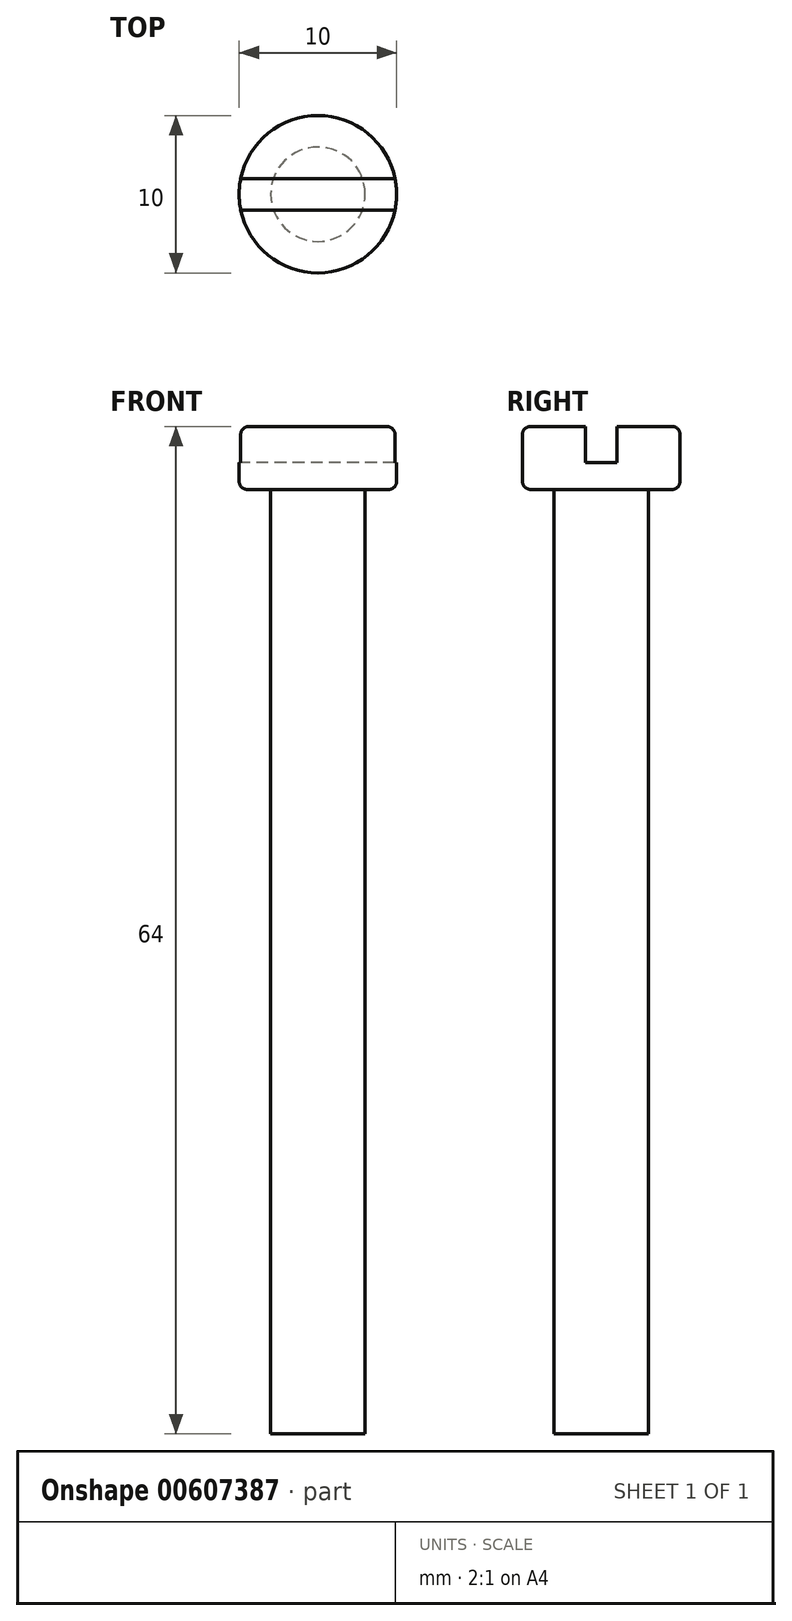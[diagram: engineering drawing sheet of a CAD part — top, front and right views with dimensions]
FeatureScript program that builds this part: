
annotation { "Feature Type Name" : "Feature", "Feature Type Description" : "" }
export const myFeature = defineFeature(function(context is Context, id is Id, definition is map)
    precondition{}
    {
        {
            var Q0;
            Q0=qCreatedBy(makeId("Top.planeOp"),FACE);
            var sketch = newSketch(context, id + "F0", { "sketchPlane" : qUnion([Q0])});
            skCircle(sketch, "E0", {"center": v(0, 0) * mm, "radius": 3 * mm});
            skSolve(sketch);
        }
        {
            var Q0;
            Q0=makeQuery(id+"F0.imprint","IMPRINT",FACE,{"disambiguationData":[TD([[makeQuery(id+"F0.imprint","IMPRINT",EDGE,{"derivedFrom":sQuery(id+"F0.wireOp",EDGE,"E0")}),1.0]])]});
            extrude(context, id + "F1", {"entities" : qUnion([Q0]), "depth" : -60 * mm, "offsetDistance" : 25 * mm});
        }
        {
            var Q0;
            Q0=makeQuery(id+"F1.opExtrude","CAP_FACE",FACE,{"disambiguationData":[OSD([sQuery(id+"F0.wireOp",EDGE,"E0")])],"isStart":true});
            var sketch = newSketch(context, id + "F2", { "sketchPlane" : qUnion([Q0])});
            skCircle(sketch, "E1", {"center": v(0, 0) * mm, "radius": 5 * mm});
            skSolve(sketch);
        }
        {
            var Q0;
            Q0 = qSketchRegion(id + "F2", true);
            extrude(context, id + "F3", {"entities" : qUnion([Q0]), "operationType" : NewBodyOperationType.ADD, "depth" : 4 * mm, "offsetDistance" : 25 * mm});
        }
        {
            var Q0;
            Q0=makeQuery(id+"F3.opExtrude","CAP_EDGE",EDGE,{"disambiguationData":[OSD([sQuery(id+"F2.wireOp",EDGE,"E1")])],"isStart":false});
            var Q1;
            Q1=makeQuery(id+"F3.opExtrude","CAP_EDGE",EDGE,{"disambiguationData":[OSD([sQuery(id+"F2.wireOp",EDGE,"E1")])],"isStart":true});
            fillet(context, id + "F4", {"entities" : qUnion([Q0, Q1]), "radius" : 0.5 * mm, "tangentPropagation" : true, "allowEdgeOverflow" : false});
        }
        {
            var Q0;
            Q0=makeQuery(id+"F3.opExtrude","CAP_FACE",FACE,{"disambiguationData":[OSD([sQuery(id+"F2.wireOp",EDGE,"E1")])],"isStart":false});
            var sketch = newSketch(context, id + "F5", { "sketchPlane" : qUnion([Q0])});
            skLineSegment(sketch, "E2.bottom", {"start": v(6.5, -1) * mm, "end": v(-6.5, -1) * mm});
            skLineSegment(sketch, "E2.top", {"start": v(6.5, 1) * mm, "end": v(-6.5, 1) * mm});
            skLineSegment(sketch, "E2.left", {"start": v(6.5, -1) * mm, "end": v(6.5, 1) * mm});
            skLineSegment(sketch, "E2.right", {"start": v(-6.5, -1) * mm, "end": v(-6.5, 1) * mm});
            skPoint(sketch, "E2.middle", {"position": v(0, 0) * mm});
            skSolve(sketch);
        }
        {
            var Q0;
            Q0 = qSketchRegion(id + "F5", true);
            extrude(context, id + "F6", {"entities" : qUnion([Q0]), "operationType" : NewBodyOperationType.REMOVE, "oppositeDirection" : true, "depth" : 2.3 * mm, "offsetDistance" : 25 * mm});
        }
    });
